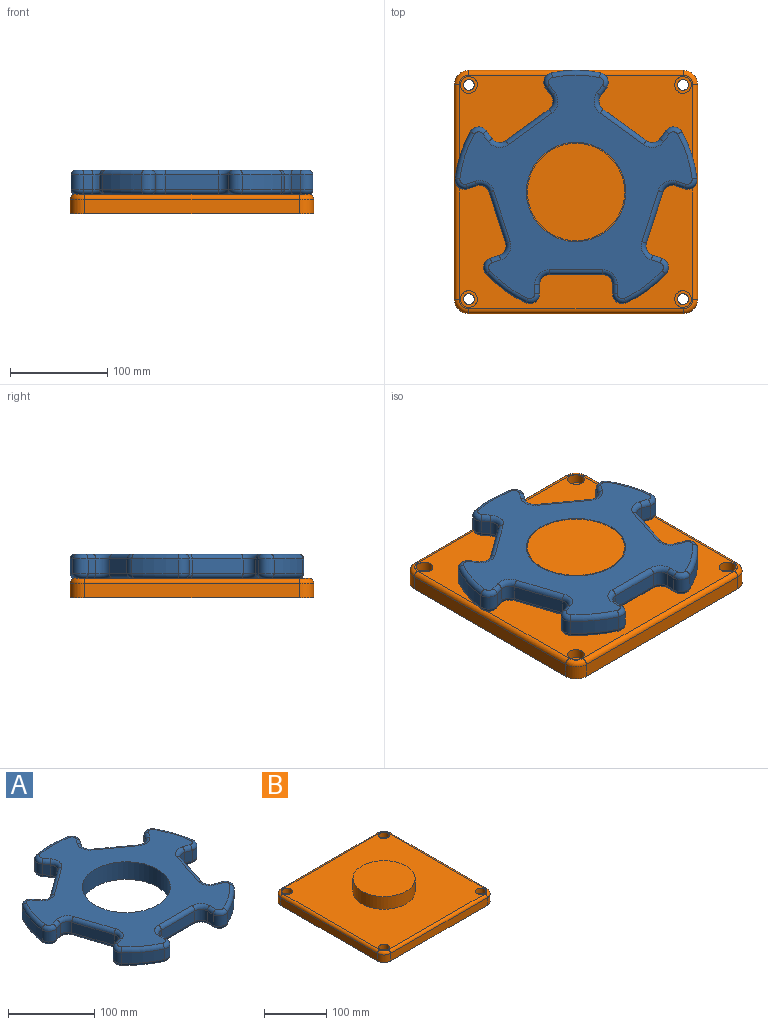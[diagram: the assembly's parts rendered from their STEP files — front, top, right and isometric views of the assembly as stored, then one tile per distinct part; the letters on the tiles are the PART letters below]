
ASSEMBLY  parts=2 mates=1
PART A: 123 faces, bbox 268.9x258.5x25 mm
  f0: plane 238.57x229.73mm, normal (0,0,1), area 21505.7mm2, adj f6,f83,f84,f85,f86,f87,f88,f89
  f1: plane 238.57x229.73mm, normal (0,0,-1), area 21505.7mm2, adj f6,f43,f44,f45,f46,f47,f48,f49
  f2: cylinder r=125mm len=47.82mm, axis (0,0,-1), area 759.5mm2, adj f34,f42,f74,f114
  f3: cylinder r=125mm len=50.29mm, axis (0,0,-1), area 759.5mm2, adj f27,f35,f75,f115
  f4: cylinder r=125mm len=47.82mm, axis (0,0,-1), area 759.5mm2, adj f20,f28,f59,f99
  f5: cylinder r=125mm len=40.68mm, axis (0,0,-1), area 759.5mm2, adj f13,f21,f43,f83
  f6: cylinder r=51mm len=102mm, axis (0,0,-1), area 8011.1mm2, adj f0,f1
  f7: cylinder r=125mm len=40.68mm, axis (0,0,-1), area 759.5mm2, adj f14,f41,f58,f98
  f8: plane 15x9.73mm, normal (-1,0,0), area 146mm2, adj f11,f14,f54,f94
  f9: plane 55x15mm, normal (0,-1,0), area 825mm2, adj f11,f12,f50,f90
  f10: plane 15x9.73mm, normal (1,0,0), area 146mm2, adj f12,f13,f46,f86
  f11: cylinder r=10mm len=15mm, axis (0,0,-1), area 235.6mm2, adj f8,f9,f52,f92
  f12: cylinder r=10mm len=15mm, axis (0,0,-1), area 235.6mm2, adj f9,f10,f48,f88
  f13: cylinder r=10mm len=15mm, axis (0,0,-1), area 299.5mm2, adj f5,f10,f44,f84
  f14: cylinder r=10mm len=15mm, axis (0,0,-1), area 299.5mm2, adj f7,f8,f56,f96
  f15: plane 15x9.26mm, normal (-0.31,0.95,0), area 146mm2, adj f18,f21,f47,f87
  f16: plane 52.31x17mm, normal (-0.95,-0.31,0), area 825mm2, adj f18,f19,f51,f91
  f17: plane 15x9.26mm, normal (0.31,-0.95,0), area 146mm2, adj f19,f20,f55,f95
  f18: cylinder r=10mm len=15mm, axis (0,0,-1), area 235.6mm2, adj f15,f16,f49,f89
  f19: cylinder r=10mm len=15mm, axis (0,0,-1), area 235.6mm2, adj f16,f17,f53,f93
  f20: cylinder r=10mm len=15mm, axis (0,0,-1), area 299.5mm2, adj f4,f17,f57,f97
  f21: cylinder r=10mm len=16.25mm, axis (0,0,-1), area 299.5mm2, adj f5,f15,f45,f85
  f22: plane 15x7.87mm, normal (0.81,0.59,0), area 146mm2, adj f25,f28,f63,f103
  f23: plane 44.5x32.33mm, normal (-0.59,0.81,0), area 825mm2, adj f25,f26,f67,f107
  f24: plane 15x7.87mm, normal (-0.81,-0.59,0), area 146mm2, adj f26,f27,f71,f111
  f25: cylinder r=10mm len=15mm, axis (0,0,-1), area 235.6mm2, adj f22,f23,f65,f105
  f26: cylinder r=10mm len=15mm, axis (0,0,-1), area 235.6mm2, adj f23,f24,f69,f109
  f27: cylinder r=10mm len=15.67mm, axis (0,0,-1), area 299.5mm2, adj f3,f24,f73,f113
  f28: cylinder r=10mm len=16.78mm, axis (0,0,-1), area 299.5mm2, adj f4,f22,f61,f101
  f29: plane 15x7.87mm, normal (0.81,-0.59,0), area 146mm2, adj f32,f35,f79,f119
  f30: plane 44.5x32.33mm, normal (0.59,0.81,0), area 825mm2, adj f32,f33,f82,f122
  f31: plane 15x7.87mm, normal (-0.81,0.59,0), area 146mm2, adj f33,f34,f78,f118
  f32: cylinder r=10mm len=15mm, axis (0,0,-1), area 235.6mm2, adj f29,f30,f81,f121
  f33: cylinder r=10mm len=15mm, axis (0,0,-1), area 235.6mm2, adj f30,f31,f80,f120
  f34: cylinder r=10mm len=16.78mm, axis (0,0,-1), area 299.5mm2, adj f2,f31,f76,f116
  f35: cylinder r=10mm len=15.67mm, axis (0,0,-1), area 299.5mm2, adj f3,f29,f77,f117
  f36: plane 15x9.26mm, normal (-0.31,-0.95,0), area 146mm2, adj f39,f42,f70,f110
  f37: plane 52.31x17mm, normal (0.95,-0.31,0), area 825mm2, adj f39,f40,f66,f106
  f38: plane 15x9.26mm, normal (0.31,0.95,0), area 146mm2, adj f40,f41,f62,f102
  f39: cylinder r=10mm len=15mm, axis (0,0,-1), area 235.6mm2, adj f36,f37,f68,f108
  f40: cylinder r=10mm len=15mm, axis (0,0,-1), area 235.6mm2, adj f37,f38,f64,f104
  f41: cylinder r=10mm len=16.25mm, axis (0,0,-1), area 299.5mm2, adj f7,f38,f60,f100
  f42: cylinder r=10mm len=15mm, axis (0,0,-1), area 299.5mm2, adj f2,f36,f72,f112
  f43: torus R=120mm, axis (0,0,1), area 391.9mm2, adj f1,f5,f44,f45
  f44: torus R=5mm, axis (0,0,1), area 128.3mm2, adj f1,f13,f43,f46
  f45: torus R=5mm, axis (0,0,1), area 128.3mm2, adj f1,f21,f43,f47
  f46: cylinder r=5mm len=9.73mm, axis (0,-1,0), area 76.4mm2, adj f1,f10,f44,f48
  f47: cylinder r=5mm len=10.8mm, axis (0.95,0.31,0), area 76.4mm2, adj f1,f15,f45,f49
  f48: torus R=15mm, axis (0,0,1), area 145.8mm2, adj f1,f12,f46,f50
  f49: torus R=15mm, axis (0,0,1), area 145.8mm2, adj f1,f18,f47,f51
  f50: cylinder r=5mm len=55mm, axis (-1,0,0), area 432mm2, adj f1,f9,f48,f52
  f51: cylinder r=5mm len=53.85mm, axis (-0.31,0.95,0), area 432mm2, adj f1,f16,f49,f53
  f52: torus R=15mm, axis (0,0,1), area 145.8mm2, adj f1,f11,f50,f54
  f53: torus R=15mm, axis (0,0,1), area 145.8mm2, adj f1,f19,f51,f55
  f54: cylinder r=5mm len=9.73mm, axis (0,1,0), area 76.4mm2, adj f1,f8,f52,f56
  f55: cylinder r=5mm len=10.8mm, axis (-0.95,-0.31,0), area 76.4mm2, adj f1,f17,f53,f57
  f56: torus R=5mm, axis (0,0,1), area 128.3mm2, adj f1,f14,f54,f58
  f57: torus R=5mm, axis (0,0,1), area 128.3mm2, adj f1,f20,f55,f59
  f58: torus R=120mm, axis (0,0,1), area 391.9mm2, adj f1,f7,f56,f60
  f59: torus R=120mm, axis (0,0,1), area 391.9mm2, adj f1,f4,f57,f61
  f60: torus R=5mm, axis (0,0,1), area 128.3mm2, adj f1,f41,f58,f62
  f61: torus R=5mm, axis (0,0,1), area 128.3mm2, adj f1,f28,f59,f63
  f62: cylinder r=5mm len=10.8mm, axis (0.95,-0.31,0), area 76.4mm2, adj f1,f38,f60,f64
  f63: cylinder r=5mm len=10.81mm, axis (0.59,-0.81,0), area 76.4mm2, adj f1,f22,f61,f65
  f64: torus R=15mm, axis (0,0,1), area 145.8mm2, adj f1,f40,f62,f66
  f65: torus R=15mm, axis (0,0,1), area 145.8mm2, adj f1,f25,f63,f67
  f66: cylinder r=5mm len=53.85mm, axis (-0.31,-0.95,0), area 432mm2, adj f1,f37,f64,f68
  f67: cylinder r=5mm len=47.44mm, axis (0.81,0.59,0), area 432mm2, adj f1,f23,f65,f69
  f68: torus R=15mm, axis (0,0,1), area 145.8mm2, adj f1,f39,f66,f70
  f69: torus R=15mm, axis (0,0,1), area 145.8mm2, adj f1,f26,f67,f71
  f70: cylinder r=5mm len=10.8mm, axis (-0.95,0.31,0), area 76.4mm2, adj f1,f36,f68,f72
  f71: cylinder r=5mm len=10.81mm, axis (-0.59,0.81,0), area 76.4mm2, adj f1,f24,f69,f73
  f72: torus R=5mm, axis (0,0,1), area 128.3mm2, adj f1,f42,f70,f74
  f73: torus R=5mm, axis (0,0,1), area 128.3mm2, adj f1,f27,f71,f75
  f74: torus R=120mm, axis (0,0,1), area 391.9mm2, adj f1,f2,f72,f76
  f75: torus R=120mm, axis (0,0,1), area 391.9mm2, adj f1,f3,f73,f77
  f76: torus R=5mm, axis (0,0,1), area 128.3mm2, adj f1,f34,f74,f78
  f77: torus R=5mm, axis (0,0,1), area 128.3mm2, adj f1,f35,f75,f79
  f78: cylinder r=5mm len=10.81mm, axis (0.59,0.81,0), area 76.4mm2, adj f1,f31,f76,f80
  f79: cylinder r=5mm len=10.81mm, axis (-0.59,-0.81,0), area 76.4mm2, adj f1,f29,f77,f81
  f80: torus R=15mm, axis (0,0,1), area 145.8mm2, adj f1,f33,f78,f82
  f81: torus R=15mm, axis (0,0,1), area 145.8mm2, adj f1,f32,f79,f82
  f82: cylinder r=5mm len=47.44mm, axis (0.81,-0.59,0), area 432mm2, adj f1,f30,f80,f81
  f83: torus R=120mm, axis (0,0,1), area 391.9mm2, adj f0,f5,f84,f85
  f84: torus R=5mm, axis (0,0,1), area 128.3mm2, adj f0,f13,f83,f86
  f85: torus R=5mm, axis (0,0,1), area 128.3mm2, adj f0,f21,f83,f87
  f86: cylinder r=5mm len=9.73mm, axis (0,1,0), area 76.4mm2, adj f0,f10,f84,f88
  f87: cylinder r=5mm len=10.8mm, axis (-0.95,-0.31,0), area 76.4mm2, adj f0,f15,f85,f89
  f88: torus R=15mm, axis (0,0,1), area 145.8mm2, adj f0,f12,f86,f90
  f89: torus R=15mm, axis (0,0,1), area 145.8mm2, adj f0,f18,f87,f91
  f90: cylinder r=5mm len=55mm, axis (1,0,0), area 432mm2, adj f0,f9,f88,f92
  f91: cylinder r=5mm len=53.85mm, axis (0.31,-0.95,0), area 432mm2, adj f0,f16,f89,f93
  f92: torus R=15mm, axis (0,0,1), area 145.8mm2, adj f0,f11,f90,f94
  f93: torus R=15mm, axis (0,0,1), area 145.8mm2, adj f0,f19,f91,f95
  f94: cylinder r=5mm len=9.73mm, axis (0,-1,0), area 76.4mm2, adj f0,f8,f92,f96
  f95: cylinder r=5mm len=10.8mm, axis (0.95,0.31,0), area 76.4mm2, adj f0,f17,f93,f97
  f96: torus R=5mm, axis (0,0,1), area 128.3mm2, adj f0,f14,f94,f98
  f97: torus R=5mm, axis (0,0,1), area 128.3mm2, adj f0,f20,f95,f99
  f98: torus R=120mm, axis (0,0,1), area 391.9mm2, adj f0,f7,f96,f100
  f99: torus R=120mm, axis (0,0,1), area 391.9mm2, adj f0,f4,f97,f101
  f100: torus R=5mm, axis (0,0,1), area 128.3mm2, adj f0,f41,f98,f102
  f101: torus R=5mm, axis (0,0,1), area 128.3mm2, adj f0,f28,f99,f103
  f102: cylinder r=5mm len=10.8mm, axis (-0.95,0.31,0), area 76.4mm2, adj f0,f38,f100,f104
  f103: cylinder r=5mm len=10.81mm, axis (-0.59,0.81,0), area 76.4mm2, adj f0,f22,f101,f105
  f104: torus R=15mm, axis (0,0,1), area 145.8mm2, adj f0,f40,f102,f106
  f105: torus R=15mm, axis (0,0,1), area 145.8mm2, adj f0,f25,f103,f107
  f106: cylinder r=5mm len=53.85mm, axis (0.31,0.95,0), area 432mm2, adj f0,f37,f104,f108
  f107: cylinder r=5mm len=47.44mm, axis (-0.81,-0.59,0), area 432mm2, adj f0,f23,f105,f109
  f108: torus R=15mm, axis (0,0,1), area 145.8mm2, adj f0,f39,f106,f110
  f109: torus R=15mm, axis (0,0,1), area 145.8mm2, adj f0,f26,f107,f111
  f110: cylinder r=5mm len=10.8mm, axis (0.95,-0.31,0), area 76.4mm2, adj f0,f36,f108,f112
  f111: cylinder r=5mm len=10.81mm, axis (0.59,-0.81,0), area 76.4mm2, adj f0,f24,f109,f113
  f112: torus R=5mm, axis (0,0,1), area 128.3mm2, adj f0,f42,f110,f114
  f113: torus R=5mm, axis (0,0,1), area 128.3mm2, adj f0,f27,f111,f115
  f114: torus R=120mm, axis (0,0,1), area 391.9mm2, adj f0,f2,f112,f116
  f115: torus R=120mm, axis (0,0,1), area 391.9mm2, adj f0,f3,f113,f117
  f116: torus R=5mm, axis (0,0,1), area 128.3mm2, adj f0,f34,f114,f118
  f117: torus R=5mm, axis (0,0,1), area 128.3mm2, adj f0,f35,f115,f119
  f118: cylinder r=5mm len=10.81mm, axis (-0.59,-0.81,0), area 76.4mm2, adj f0,f31,f116,f120
  f119: cylinder r=5mm len=10.81mm, axis (0.59,0.81,0), area 76.4mm2, adj f0,f29,f117,f121
  f120: torus R=15mm, axis (0,0,1), area 145.8mm2, adj f0,f33,f118,f122
  f121: torus R=15mm, axis (0,0,1), area 145.8mm2, adj f0,f32,f119,f122
  f122: cylinder r=5mm len=47.44mm, axis (-0.81,0.59,0), area 432mm2, adj f0,f30,f120,f121
PART B: 32 faces, bbox 252.5x252.5x45 mm
  f0: plane 220x15mm, normal (1,0,0), area 3300mm2, adj f5,f8,f11,f27
  f1: plane 220x15mm, normal (0,1,0), area 3300mm2, adj f5,f8,f9,f31
  f2: plane 220x15mm, normal (-1,0,0), area 3300mm2, adj f5,f9,f10,f28
  f3: plane 220x15mm, normal (0,-1,0), area 3300mm2, adj f5,f10,f11,f24
  f4: plane 240x240mm, normal (0,0,1), area 48725.4mm2, adj f6,f14,f17,f20,f23,f24,f25,f26
  f5: plane 250x250mm, normal (0,0,-1), area 61926.7mm2, adj f0,f1,f2,f3,f8,f9,f10,f11
  f6: cylinder r=50mm len=100mm, axis (0,0,-1), area 7854mm2, adj f4,f7
  f7: plane 100x100mm, normal (0,0,1), area 7854mm2, adj f6
  f8: cylinder r=15mm len=15mm, axis (0,0,-1), area 353.4mm2, adj f0,f1,f5,f29
  f9: cylinder r=15mm len=15mm, axis (0,0,1), area 353.4mm2, adj f1,f2,f5,f30
  f10: cylinder r=15mm len=15mm, axis (0,0,-1), area 353.4mm2, adj f2,f3,f5,f26
  f11: cylinder r=15mm len=15mm, axis (0,0,1), area 353.4mm2, adj f0,f3,f5,f25
  f12: cylinder r=5.5mm len=11mm, axis (0,0,1), area 345.6mm2, adj f5,f13
  f13: plane 17.25x17.25mm, normal (0,0,1), area 138.7mm2, adj f12,f14
  f14: cylinder r=8.62mm len=17.25mm, axis (0,0,1), area 541.9mm2, adj f4,f13
  f15: cylinder r=5.5mm len=11mm, axis (0,0,1), area 345.6mm2, adj f5,f16
  f16: plane 17.25x17.25mm, normal (0,0,1), area 138.7mm2, adj f15,f17
  f17: cylinder r=8.62mm len=17.25mm, axis (0,0,1), area 541.9mm2, adj f4,f16
  f18: cylinder r=5.5mm len=11mm, axis (0,0,1), area 345.6mm2, adj f5,f19
  f19: plane 17.25x17.25mm, normal (0,0,1), area 138.7mm2, adj f18,f20
  f20: cylinder r=8.62mm len=17.25mm, axis (0,0,1), area 541.9mm2, adj f4,f19
  f21: cylinder r=5.5mm len=11mm, axis (0,0,1), area 345.6mm2, adj f5,f22
  f22: plane 17.25x17.25mm, normal (0,0,1), area 138.7mm2, adj f21,f23
  f23: cylinder r=8.62mm len=17.25mm, axis (0,0,1), area 541.9mm2, adj f4,f22
  f24: cylinder r=5mm len=220mm, axis (-1,0,0), area 1727.9mm2, adj f3,f4,f25,f26
  f25: torus R=10mm, axis (0,0,1), area 162.6mm2, adj f4,f11,f24,f27
  f26: torus R=10mm, axis (0,0,1), area 162.6mm2, adj f4,f10,f24,f28
  f27: cylinder r=5mm len=220mm, axis (0,-1,0), area 1727.9mm2, adj f0,f4,f25,f29
  f28: cylinder r=5mm len=220mm, axis (0,1,0), area 1727.9mm2, adj f2,f4,f26,f30
  f29: torus R=10mm, axis (0,0,1), area 162.6mm2, adj f4,f8,f27,f31
  f30: torus R=10mm, axis (0,0,1), area 162.6mm2, adj f4,f9,f28,f31
  f31: cylinder r=5mm len=220mm, axis (1,0,0), area 1727.9mm2, adj f1,f4,f29,f30
PLACE A at identity
PLACE B at identity fixed
MATE revolute B.f6 <-> A.f2  axis (0,0,-1) through (0,0,20)mm
